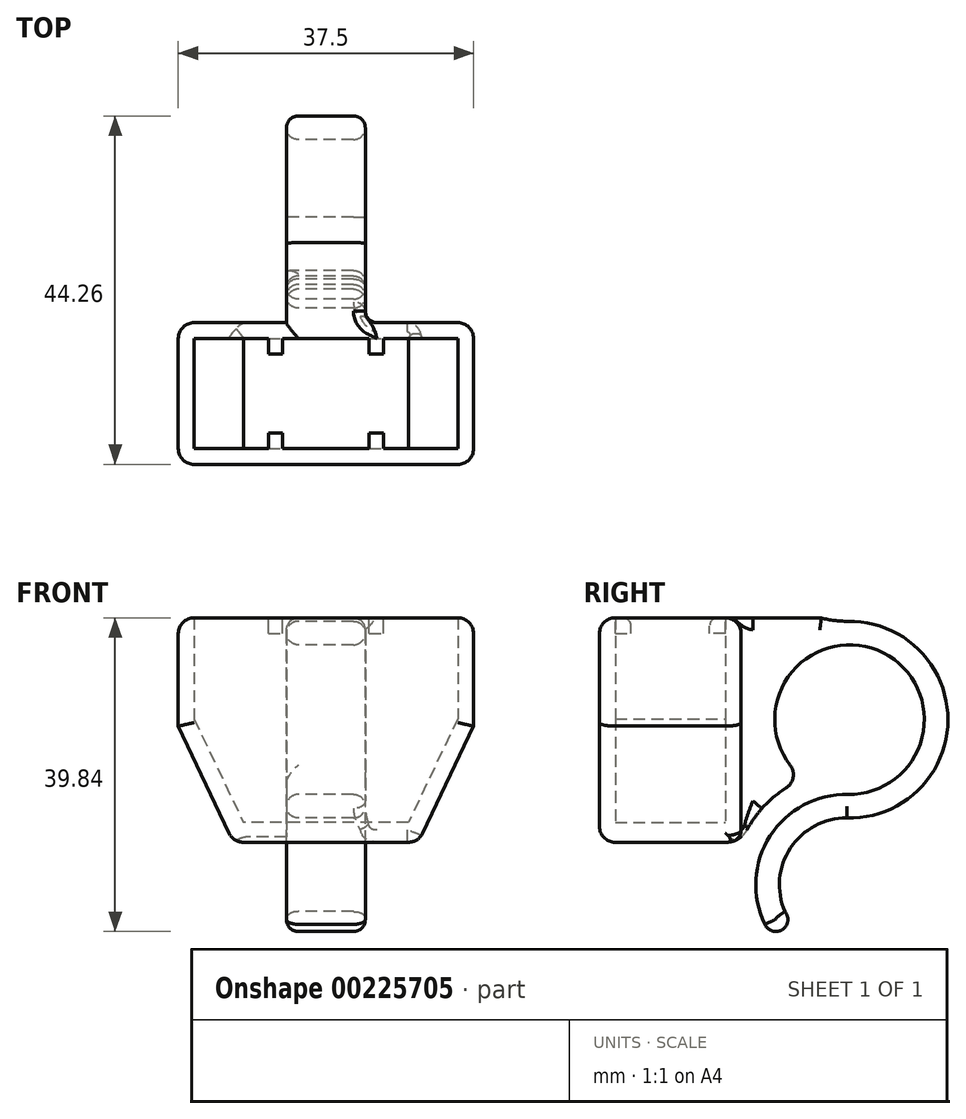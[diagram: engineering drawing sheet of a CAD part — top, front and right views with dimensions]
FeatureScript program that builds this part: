
annotation { "Feature Type Name" : "Feature", "Feature Type Description" : "" }
export const myFeature = defineFeature(function(context is Context, id is Id, definition is map)
    precondition{}
    {
        {
            var Q0;
            Q0=qCreatedBy(makeId("Front.planeOp"),FACE);
            var sketch = newSketch(context, id + "F0", { "sketchPlane" : qUnion([Q0])});
            skLineSegment(sketch, "E0.bottom", {"start": v(-18.75, 13.75) * mm, "end": v(18.75, 13.75) * mm});
            skLineSegment(sketch, "E0.left", {"start": v(-18.75, 13.75) * mm, "end": v(-18.75, 0) * mm});
            skLineSegment(sketch, "E0.right", {"start": v(18.75, 13.75) * mm, "end": v(18.75, 0) * mm});
            skLineSegment(sketch, "E1.bottom", {"start": v(11.75, -14.75) * mm, "end": v(-11.75, -14.75) * mm});
            skLineSegment(sketch, "E2", {"start": v(-18.75, 0) * mm, "end": v(-11.75, -14.75) * mm});
            skLineSegment(sketch, "E3", {"start": v(18.75, 0) * mm, "end": v(11.75, -14.75) * mm});
            skSolve(sketch);
        }
        {
            var Q0;
            Q0=qCreatedBy(makeId("Front.planeOp"),FACE);
            var sketch = newSketch(context, id + "F1", { "sketchPlane" : qUnion([Q0])});
            skLineSegment(sketch, "E4.0", {"start": v(-16.75, 13.75) * mm, "end": v(16.75, 13.75) * mm});
            skLineSegment(sketch, "E4.1", {"start": v(-16.75, 0.94) * mm, "end": v(-10.49, -12.26) * mm});
            skLineSegment(sketch, "E4.2", {"start": v(10.49, -12.26) * mm, "end": v(-10.49, -12.26) * mm});
            skLineSegment(sketch, "E4.3", {"start": v(-16.75, 13.75) * mm, "end": v(-16.75, 0.94) * mm});
            skLineSegment(sketch, "E4.4", {"start": v(16.75, 0.94) * mm, "end": v(10.49, -12.26) * mm});
            skLineSegment(sketch, "E4.5", {"start": v(16.75, 13.75) * mm, "end": v(16.75, 0.94) * mm});
            skSolve(sketch);
        }
        {
            var Q0;
            Q0 = qSketchRegion(id + "F0", true);
            extrude(context, id + "F2", {"entities" : qUnion([Q0]), "endBound" : BoundingType.SYMMETRIC, "depth" : 18 * mm});
        }
        {
            var Q0;
            Q0 = qSketchRegion(id + "F1", true);
            extrude(context, id + "F3", {"entities" : qUnion([Q0]), "operationType" : NewBodyOperationType.REMOVE, "endBound" : BoundingType.SYMMETRIC, "depth" : 14 * mm});
        }
        {
            var Q0;
            Q0=qCreatedBy(makeId("Right.planeOp"),FACE);
            var sketch = newSketch(context, id + "F4", { "sketchPlane" : qUnion([Q0])});
            skLineSegment(sketch, "E5.right", {"start": v(9, 13.75) * mm, "end": v(9, -14.75) * mm});
            skArc(sketch, "E6.0", {"start": v(16.97, -6.7) * mm, "mid": v(12.16, -9.9) * mm, "end": v(9.02, -14.75) * mm});
            skArc(sketch, "E7", {"start": v(12, -25.18) * mm, "mid": v(14.22, -25.86) * mm, "end": v(14.56, -23.56) * mm});
            skLineSegment(sketch, "E8", {"start": v(9, 13.75) * mm, "end": v(19.2, 13.75) * mm});
            skArc(sketch, "E9", {"start": v(22.42, -11.67) * mm, "mid": v(35.26, 0.78) * mm, "end": v(22.52, 13.33) * mm});
            skArc(sketch, "E10", {"start": v(22.58, -8.67) * mm, "mid": v(12.67, -13.96) * mm, "end": v(12, -25.18) * mm});
            skArc(sketch, "E11", {"start": v(19.2, 13.75) * mm, "mid": v(20.84, 13.42) * mm, "end": v(22.52, 13.33) * mm});
            skArc(sketch, "E12", {"start": v(22.42, -11.67) * mm, "mid": v(15.26, -15.48) * mm, "end": v(14.56, -23.56) * mm});
            skArc(sketch, "E13", {"start": v(22.58, -8.67) * mm, "mid": v(25.9, 9.8) * mm, "end": v(16.97, -6.7) * mm});
            skLineSegment(sketch, "E14", {"start": v(9, -14.75) * mm, "end": v(9.02, -14.75) * mm});
            skSolve(sketch);
        }
        {
            var Q0;
            Q0 = qSketchRegion(id + "F4", true);
            extrude(context, id + "F5", {"entities" : qUnion([Q0]), "operationType" : NewBodyOperationType.ADD, "endBound" : BoundingType.SYMMETRIC, "offsetDistance" : 25 * mm, "depth" : 10 * mm});
        }
        {
            var Q0;
            Q0=makeQuery(id+"F5.boolean.opBoolean","MERGE",FACE,{"derivedFrom":[makeQuery(id+"F2.opExtrude","SWEPT_FACE",FACE,{"disambiguationData":[OSD([sQuery(id+"F0.wireOp",EDGE,"E0.bottom")])]}),makeQuery(id+"F5.opExtrude","SWEPT_FACE",FACE,{"disambiguationData":[OSD([sQuery(id+"F4.wireOp",EDGE,"E8")])]})]});
            var sketch = newSketch(context, id + "F6", { "sketchPlane" : qUnion([Q0])});
            skLineSegment(sketch, "E15.bottom", {"start": v(-7.3, 7) * mm, "end": v(-5.5, 7) * mm});
            skLineSegment(sketch, "E15.top", {"start": v(-7.3, 5) * mm, "end": v(-5.5, 5) * mm});
            skLineSegment(sketch, "E15.left", {"start": v(-7.3, 7) * mm, "end": v(-7.3, 5) * mm});
            skLineSegment(sketch, "E15.right", {"start": v(7.3, 7) * mm, "end": v(7.3, 5) * mm});
            skLineSegment(sketch, "E16.left", {"start": v(-5.5, 7) * mm, "end": v(-5.5, 5) * mm});
            skLineSegment(sketch, "E16.right", {"start": v(5.5, 7) * mm, "end": v(5.5, 5) * mm});
            skLineSegment(sketch, "E17.trimOffspring", {"start": v(5.5, 7) * mm, "end": v(7.3, 7) * mm});
            skLineSegment(sketch, "E18.trimOffspring", {"start": v(5.5, 5) * mm, "end": v(7.3, 5) * mm});
            skLineSegment(sketch, "E19.MirrorCS", {"start": v(-7.3, -5) * mm, "end": v(-5.5, -5) * mm});
            skLineSegment(sketch, "E20.MirrorCS", {"start": v(-7.3, -7) * mm, "end": v(-7.3, -5) * mm});
            skLineSegment(sketch, "E21.MirrorCS", {"start": v(7.3, -7) * mm, "end": v(7.3, -5) * mm});
            skLineSegment(sketch, "E22.MirrorCS", {"start": v(-5.5, -7) * mm, "end": v(-5.5, -5) * mm});
            skLineSegment(sketch, "E23.MirrorCS", {"start": v(5.5, -5) * mm, "end": v(7.3, -5) * mm});
            skLineSegment(sketch, "E24.MirrorCS", {"start": v(5.5, -7) * mm, "end": v(5.5, -5) * mm});
            skSolve(sketch);
        }
        {
            var Q0;
            Q0 = qSketchRegion(id + "F6", true);
            var Q1;
            Q1=makeQuery(id+"F6.imprint","IMPRINT",FACE,{"disambiguationData":[TD([[makeQuery(id+"F6.imprint","IMPRINT",EDGE,{"derivedFrom":sQuery(id+"F6.wireOp",EDGE,"E19.MirrorCS")}),-1.0]])]});
            var Q2;
            {var subQ0=sQuery(id+"F6.wireOp",EDGE,"E21.MirrorCS");Q2=makeQuery(id+"F6.imprint","IMPRINT",FACE,{"disambiguationData":[TD([[makeQuery(id+"F6.imprint","IMPRINT",EDGE,{"derivedFrom":subQ0}),1.0]])]});}
            extrude(context, id + "F7", {"entities" : qUnion([Q0, Q1, Q2]), "operationType" : NewBodyOperationType.ADD, "oppositeDirection" : true, "depth" : 2 * mm});
        }
        {
            var Q0;
            Q0=makeQuery(id+"F2.opExtrude","CAP_EDGE",EDGE,{"disambiguationData":[OSD([sQuery(id+"F0.wireOp",EDGE,"E0.left")])],"isStart":false});
            var Q1;
            Q1=makeQuery(id+"F2.opExtrude","CAP_EDGE",EDGE,{"disambiguationData":[OSD([sQuery(id+"F0.wireOp",EDGE,"E0.left")])],"isStart":true});
            var Q2;
            Q2=makeQuery(id+"F2.opExtrude","CAP_EDGE",EDGE,{"disambiguationData":[OSD([sQuery(id+"F0.wireOp",EDGE,"E2")])],"isStart":false});
            var Q3;
            Q3=makeQuery(id+"F2.opExtrude","CAP_EDGE",EDGE,{"disambiguationData":[OSD([sQuery(id+"F0.wireOp",EDGE,"E1.bottom")])],"isStart":false});
            var Q4;
            Q4=makeQuery(id+"F2.opExtrude","SWEPT_EDGE",EDGE,{"disambiguationData":[OSD([sQuery(id+"F0.wireOp",EDGE,"E1.bottom"),sQuery(id+"F0.wireOp",EDGE,"E2")])]});
            var Q5;
            Q5=makeQuery(id+"F2.opExtrude","CAP_EDGE",EDGE,{"disambiguationData":[OSD([sQuery(id+"F0.wireOp",EDGE,"E3")])],"isStart":false});
            var Q6;
            Q6=makeQuery(id+"F2.opExtrude","CAP_EDGE",EDGE,{"disambiguationData":[OSD([sQuery(id+"F0.wireOp",EDGE,"E0.right")])],"isStart":false});
            var Q7;
            Q7=makeQuery(id+"F2.opExtrude","CAP_EDGE",EDGE,{"disambiguationData":[OSD([sQuery(id+"F0.wireOp",EDGE,"E0.right")])],"isStart":true});
            var Q8;
            Q8=makeQuery(id+"F2.opExtrude","CAP_EDGE",EDGE,{"disambiguationData":[OSD([sQuery(id+"F0.wireOp",EDGE,"E3")])],"isStart":true});
            var Q9;
            Q9=makeQuery(id+"F2.opExtrude","SWEPT_EDGE",EDGE,{"disambiguationData":[OSD([sQuery(id+"F0.wireOp",EDGE,"E0.bottom"),sQuery(id+"F0.wireOp",EDGE,"E0.left")])]});
            var Q10;
            Q10=makeQuery(id+"F2.opExtrude","CAP_EDGE",EDGE,{"disambiguationData":[OSD([sQuery(id+"F0.wireOp",EDGE,"E0.bottom")])],"isStart":false});
            var Q11;
            Q11=makeQuery(id+"F2.opExtrude","SWEPT_EDGE",EDGE,{"disambiguationData":[OSD([sQuery(id+"F0.wireOp",EDGE,"E0.bottom"),sQuery(id+"F0.wireOp",EDGE,"E0.right")])]});
            var Q12;
            Q12=makeQuery(id+"F2.opExtrude","CAP_EDGE",EDGE,{"disambiguationData":[OSD([sQuery(id+"F0.wireOp",EDGE,"E2")])],"isStart":true});
            var Q13;
            Q13=makeQuery(id+"F2.opExtrude","SWEPT_EDGE",EDGE,{"disambiguationData":[OSD([sQuery(id+"F0.wireOp",EDGE,"E1.bottom"),sQuery(id+"F0.wireOp",EDGE,"E3")])]});
            var Q14;
            Q14=qNothing();
            var Q15;
            {var subQ0=sQuery(id+"F0.wireOp",EDGE,"E0.right");var subQ2=sQuery(id+"F0.wireOp",EDGE,"E0.bottom");Q15=makeQuery(id+"F5.boolean.opBoolean","SPLIT",EDGE,{"disambiguationData":[TD([makeQuery(id+"F2.opExtrude","SWEPT_FACE",FACE,{"disambiguationData":[OSD([subQ0])]})])],"derivedFrom":makeQuery(id+"F2.opExtrude","CAP_EDGE",EDGE,{"disambiguationData":[OSD([subQ2])],"isStart":true})});}
            var Q16;
            {var subQ1=sQuery(id+"F0.wireOp",EDGE,"E0.bottom");var subQ2=sQuery(id+"F0.wireOp",EDGE,"E0.left");Q16=makeQuery(id+"F5.boolean.opBoolean","SPLIT",EDGE,{"disambiguationData":[TD([makeQuery(id+"F2.opExtrude","SWEPT_FACE",FACE,{"disambiguationData":[OSD([subQ2])]})])],"derivedFrom":makeQuery(id+"F2.opExtrude","CAP_EDGE",EDGE,{"disambiguationData":[OSD([subQ1])],"isStart":true})});}
            var Q17;
            Q17=makeQuery(id+"F5.opExtrude","SWEPT_EDGE",EDGE,{"disambiguationData":[OSD([sQuery(id+"F4.wireOp",EDGE,"E6.0"),sQuery(id+"F4.wireOp",EDGE,"E13")])]});
            fillet(context, id + "F8", {"entities" : qUnion([Q0, Q1, Q2, Q3, Q4, Q5, Q6, Q7, Q8, Q9, Q10, Q11, Q12, Q13, Q14, Q15, Q16, Q17]), "radius" : 2 * mm, "tangentPropagation" : true, "defaultsChanged" : false, "vertexSettings" : [], "allowEdgeOverflow" : false});
        }
        {
            var Q0;
            Q0=makeQuery(id+"F5.opExtrude","CAP_EDGE",EDGE,{"disambiguationData":[OSD([sQuery(id+"F4.wireOp",EDGE,"E5.right")])],"isStart":false});
            var Q1;
            Q1=makeQuery(id+"F5.opExtrude","CAP_EDGE",EDGE,{"disambiguationData":[OSD([sQuery(id+"F4.wireOp",EDGE,"E5.right")])],"isStart":true});
            fillet(context, id + "F9", {"entities" : qUnion([Q0, Q1]), "radius" : 1.5 * mm, "tangentPropagation" : true, "defaultsChanged" : true, "vertexSettings" : [], "allowEdgeOverflow" : false});
        }
        {
            var Q0;
            Q0=makeQuery(id+"F7.opExtrude","CAP_EDGE",EDGE,{"disambiguationData":[OSD([sQuery(id+"F6.wireOp",EDGE,"E23.MirrorCS")])],"isStart":true});
            var Q1;
            Q1=makeQuery(id+"F7.opExtrude","CAP_EDGE",EDGE,{"disambiguationData":[OSD([sQuery(id+"F6.wireOp",EDGE,"E19.MirrorCS")])],"isStart":true});
            var Q2;
            Q2=makeQuery(id+"F7.opExtrude","CAP_EDGE",EDGE,{"disambiguationData":[OSD([sQuery(id+"F6.wireOp",EDGE,"E18.trimOffspring")])],"isStart":true});
            var Q3;
            Q3=makeQuery(id+"F7.opExtrude","CAP_EDGE",EDGE,{"disambiguationData":[OSD([sQuery(id+"F6.wireOp",EDGE,"E15.top")])],"isStart":true});
            fillet(context, id + "F10", {"entities" : qUnion([Q0, Q1, Q2, Q3]), "radius" : 1 * mm, "tangentPropagation" : true, "defaultsChanged" : false, "vertexSettings" : [], "allowEdgeOverflow" : false});
        }
        {
            var Q0;
            Q0=makeQuery(id+"F5.opExtrude","SWEPT_EDGE",EDGE,{"disambiguationData":[OSD([sQuery(id+"F4.wireOp",EDGE,"E5.right"),sQuery(id+"F4.wireOp",EDGE,"E6.0")])]});
            fillet(context, id + "F11", {"entities" : qUnion([Q0]), "radius" : 3 * mm, "defaultsChanged" : true, "vertexSettings" : [], "allowEdgeOverflow" : false});
        }
        {
            var Q0;
            Q0=makeQuery(id+"F5.opExtrude","CAP_EDGE",EDGE,{"disambiguationData":[OSD([sQuery(id+"F4.wireOp",EDGE,"E6.0")])],"isStart":false});
            var Q1;
            {var subQ0=sQuery(id+"F4.wireOp",EDGE,"E13");var subQ1=sQuery(id+"F4.wireOp",EDGE,"E6.0");Q1=makeQuery(id+"F8.opFillet","BLEND_EDGE",EDGE,{"blendedFrom":[makeQuery(id+"F5.opExtrude","SWEPT_EDGE",EDGE,{"disambiguationData":[OSD([subQ1,subQ0])]}),makeQuery(id+"F5.opExtrude","CAP_FACE",FACE,{"disambiguationData":[OSD([sQuery(id+"F4.wireOp",EDGE,"E5.right"),subQ1,sQuery(id+"F4.wireOp",EDGE,"E7"),sQuery(id+"F4.wireOp",EDGE,"E8"),sQuery(id+"F4.wireOp",EDGE,"E9"),sQuery(id+"F4.wireOp",EDGE,"E10"),sQuery(id+"F4.wireOp",EDGE,"E11"),sQuery(id+"F4.wireOp",EDGE,"E12"),subQ0,sQuery(id+"F4.wireOp",EDGE,"E14")])],"isStart":false})],"blendedInto":[makeQuery(id+"F5.opExtrude","CAP_FACE",FACE,{"disambiguationData":[OSD([sQuery(id+"F4.wireOp",EDGE,"E5.right"),subQ1,sQuery(id+"F4.wireOp",EDGE,"E7"),sQuery(id+"F4.wireOp",EDGE,"E8"),sQuery(id+"F4.wireOp",EDGE,"E9"),sQuery(id+"F4.wireOp",EDGE,"E10"),sQuery(id+"F4.wireOp",EDGE,"E11"),sQuery(id+"F4.wireOp",EDGE,"E12"),subQ0,sQuery(id+"F4.wireOp",EDGE,"E14")])],"isStart":false})]});}
            var Q2;
            Q2=makeQuery(id+"F5.opExtrude","CAP_EDGE",EDGE,{"disambiguationData":[OSD([sQuery(id+"F4.wireOp",EDGE,"E13")])],"isStart":false});
            var Q3;
            Q3=makeQuery(id+"F5.opExtrude","CAP_EDGE",EDGE,{"disambiguationData":[OSD([sQuery(id+"F4.wireOp",EDGE,"E7")])],"isStart":false});
            var Q4;
            Q4=makeQuery(id+"F5.opExtrude","CAP_EDGE",EDGE,{"disambiguationData":[OSD([sQuery(id+"F4.wireOp",EDGE,"E12")])],"isStart":false});
            var Q5;
            Q5=makeQuery(id+"F5.opExtrude","CAP_EDGE",EDGE,{"disambiguationData":[OSD([sQuery(id+"F4.wireOp",EDGE,"E12")])],"isStart":true});
            var Q6;
            Q6=makeQuery(id+"F5.opExtrude","CAP_EDGE",EDGE,{"disambiguationData":[OSD([sQuery(id+"F4.wireOp",EDGE,"E7")])],"isStart":true});
            var Q7;
            Q7=makeQuery(id+"F5.opExtrude","CAP_EDGE",EDGE,{"disambiguationData":[OSD([sQuery(id+"F4.wireOp",EDGE,"E9")])],"isStart":true});
            var Q8;
            Q8=makeQuery(id+"F5.opExtrude","CAP_EDGE",EDGE,{"disambiguationData":[OSD([sQuery(id+"F4.wireOp",EDGE,"E9")])],"isStart":false});
            var Q9;
            Q9=makeQuery(id+"F5.opExtrude","CAP_EDGE",EDGE,{"disambiguationData":[OSD([sQuery(id+"F4.wireOp",EDGE,"E11")])],"isStart":false});
            var Q10;
            Q10=makeQuery(id+"F5.opExtrude","CAP_EDGE",EDGE,{"disambiguationData":[OSD([sQuery(id+"F4.wireOp",EDGE,"E8")])],"isStart":false});
            var Q11;
            Q11=makeQuery(id+"F5.opExtrude","CAP_EDGE",EDGE,{"disambiguationData":[OSD([sQuery(id+"F4.wireOp",EDGE,"E8")])],"isStart":true});
            var Q12;
            Q12=makeQuery(id+"F5.opExtrude","CAP_EDGE",EDGE,{"disambiguationData":[OSD([sQuery(id+"F4.wireOp",EDGE,"E11")])],"isStart":true});
            fillet(context, id + "F12", {"entities" : qUnion([Q0, Q1, Q2, Q3, Q4, Q5, Q6, Q7, Q8, Q9, Q10, Q11, Q12]), "tangentPropagation" : true, "radius" : 1.5 * mm, "defaultsChanged" : true, "vertexSettings" : [], "allowEdgeOverflow" : false});
        }
    });
